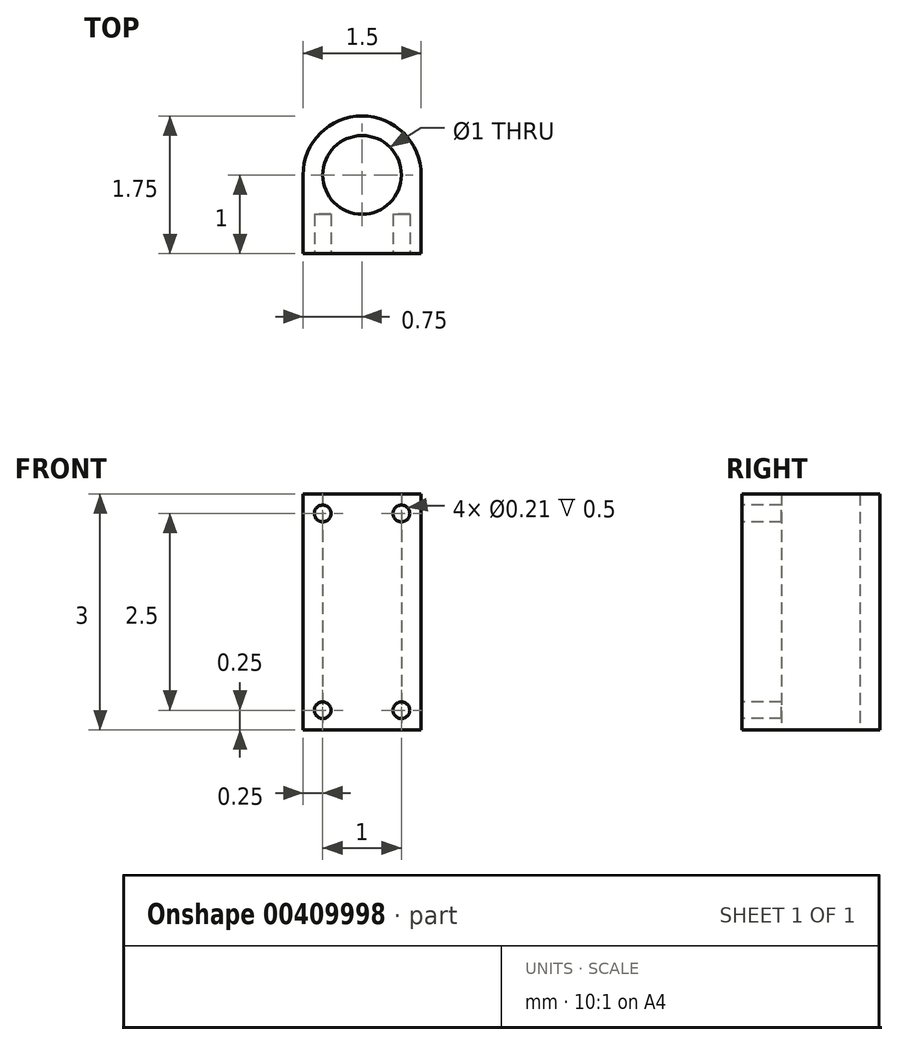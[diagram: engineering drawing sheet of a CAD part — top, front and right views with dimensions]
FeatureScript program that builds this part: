
annotation { "Feature Type Name" : "Feature", "Feature Type Description" : "" }
export const myFeature = defineFeature(function(context is Context, id is Id, definition is map)
    precondition{}
    {
        {
            var Q0;
            Q0=qCreatedBy(makeId("Top.planeOp"),FACE);
            var sketch = newSketch(context, id + "F0", { "sketchPlane" : qUnion([Q0])});
            skLineSegment(sketch, "E0.top", {"start": v(-0.75, 0) * mm, "end": v(0.75, 0) * mm});
            skLineSegment(sketch, "E0.left", {"start": v(-0.75, 1) * mm, "end": v(-0.75, 0) * mm});
            skLineSegment(sketch, "E0.right", {"start": v(0.75, 1) * mm, "end": v(0.75, 0) * mm});
            skArc(sketch, "E1", {"start": v(0.75, 1) * mm, "mid": v(0, 1.75) * mm, "end": v(-0.75, 1) * mm});
            skPoint(sketch, "E1.third.point", {"position": v(0, 1.75) * mm});
            skPoint(sketch, "E1.third.point.positionSnap0", {"position": v(0, 1) * mm});
            skCircle(sketch, "E2", {"center": v(0, 1) * mm, "radius": 0.5 * mm});
            skSolve(sketch);
        }
        {
            var Q0;
            Q0 = qSketchRegion(id + "F0", true);
            extrude(context, id + "F1", {"entities" : qUnion([Q0]), "depth" : 3 * mm});
        }
        {
            var Q0;
            Q0=makeQuery(id+"F1.opExtrude","SWEPT_FACE",FACE,{"disambiguationData":[OSD([sQuery(id+"F0.wireOp",EDGE,"E0.top")])]});
            var sketch = newSketch(context, id + "F2", { "sketchPlane" : qUnion([Q0])});
            skLineSegment(sketch, "E3.bottom", {"start": v(-0.5, 2.75) * mm, "end": v(0.5, 2.75) * mm, "construction": true});
            skLineSegment(sketch, "E3.top", {"start": v(-0.5, 0.25) * mm, "end": v(0.5, 0.25) * mm, "construction": true});
            skLineSegment(sketch, "E3.left", {"start": v(-0.5, 2.75) * mm, "end": v(-0.5, 0.25) * mm, "construction": true});
            skLineSegment(sketch, "E3.right", {"start": v(0.5, 2.75) * mm, "end": v(0.5, 0.25) * mm, "construction": true});
            skCircle(sketch, "E4", {"center": v(-0.5, 2.75) * mm, "radius": 0.1 * mm});
            skCircle(sketch, "E5", {"center": v(0.5, 0.25) * mm, "radius": 0.1 * mm});
            skCircle(sketch, "E6", {"center": v(-0.5, 0.25) * mm, "radius": 0.1 * mm});
            skCircle(sketch, "E7", {"center": v(0.5, 2.75) * mm, "radius": 0.1 * mm});
            skSolve(sketch);
        }
        {
            var Q0;
            Q0 = qSketchRegion(id + "F2", true);
            extrude(context, id + "F3", {"entities" : qUnion([Q0]), "operationType" : NewBodyOperationType.REMOVE, "oppositeDirection" : true, "depth" : 0.5 * mm});
        }
    });
